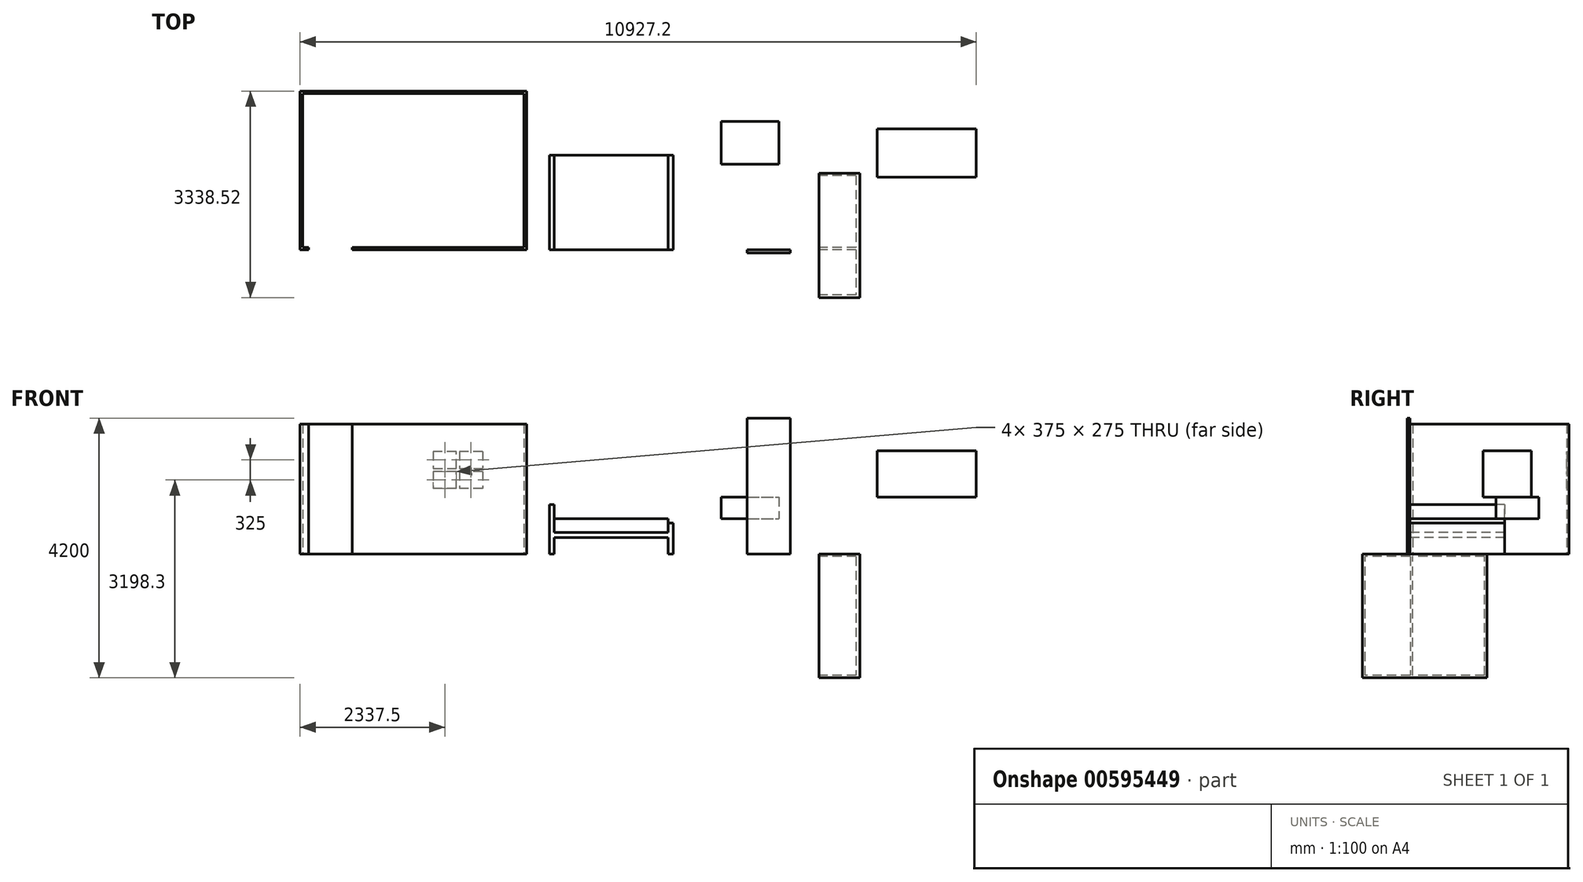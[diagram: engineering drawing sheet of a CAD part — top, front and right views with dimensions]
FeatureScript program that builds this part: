
annotation { "Feature Type Name" : "Feature", "Feature Type Description" : "" }
export const myFeature = defineFeature(function(context is Context, id is Id, definition is map)
    precondition{}
    {
        {
            var Q0;
            Q0=qCreatedBy(makeId("Top.planeOp"),FACE);
            var sketch = newSketch(context, id + "F0", { "sketchPlane" : qUnion([Q0])});
            skLineSegment(sketch, "E0", {"start": v(40, -40) * mm, "end": v(40, -2529) * mm});
            skLineSegment(sketch, "E1", {"start": v(40, -2529) * mm, "end": v(140, -2529) * mm});
            skLineSegment(sketch, "E2", {"start": v(140, -2529) * mm, "end": v(140, -2569) * mm});
            skLineSegment(sketch, "E3", {"start": v(840, -2529) * mm, "end": v(3620, -2529) * mm});
            skLineSegment(sketch, "E4", {"start": v(3620, -2529) * mm, "end": v(3620, -40) * mm});
            skLineSegment(sketch, "E5", {"start": v(3620, -40) * mm, "end": v(40, -40) * mm});
            skLineSegment(sketch, "E6.0", {"start": v(0, -2569) * mm, "end": v(140, -2569) * mm});
            skLineSegment(sketch, "E6.1", {"start": v(0, 0) * mm, "end": v(0, -2569) * mm});
            skLineSegment(sketch, "E6.2", {"start": v(840, -2569) * mm, "end": v(840, -2529) * mm});
            skLineSegment(sketch, "E6.3", {"start": v(840, -2569) * mm, "end": v(3660, -2569) * mm});
            skLineSegment(sketch, "E6.4", {"start": v(3660, -2569) * mm, "end": v(3660, 0) * mm});
            skLineSegment(sketch, "E6.5", {"start": v(3660, 0) * mm, "end": v(0, 0) * mm});
            skLineSegment(sketch, "E7", {"start": v(77.43, -3008.4) * mm, "end": v(77.43, -5573.82) * mm});
            skLineSegment(sketch, "E8", {"start": v(77.43, -5573.82) * mm, "end": v(3731.87, -5573.82) * mm});
            skLineSegment(sketch, "E9", {"start": v(3731.87, -5573.82) * mm, "end": v(3731.87, -3584.3) * mm});
            skLineSegment(sketch, "E10", {"start": v(3731.87, -3584.3) * mm, "end": v(865.25, -3584.3) * mm});
            skLineSegment(sketch, "E11", {"start": v(865.25, -3584.3) * mm, "end": v(865.25, -3010.27) * mm});
            skSolve(sketch);
        }
        {
            var Q0;
            Q0 = qSketchRegion(id + "F0", true);
            extrude(context, id + "F1", {"entities" : qUnion([Q0]), "depth" : 2100 * mm, "offsetDistance" : 25 * mm});
        }
        {
            var Q0;
            Q0=makeQuery(id+"F1.opExtrude","SWEPT_FACE",FACE,{"disambiguationData":[OSD([sQuery(id+"F0.wireOp",EDGE,"E6.3")])]});
            var sketch = newSketch(context, id + "F2", { "sketchPlane" : qUnion([Q0])});
            skLineSegment(sketch, "E12", {"start": v(4029.05, 800) * mm, "end": v(4029.05, 0) * mm});
            skLineSegment(sketch, "E13", {"start": v(4029.05, 0) * mm, "end": v(4109.05, 0) * mm});
            skLineSegment(sketch, "E14", {"start": v(4109.05, 0) * mm, "end": v(4109.05, 270) * mm});
            skLineSegment(sketch, "E15", {"start": v(4109.05, 270) * mm, "end": v(5949.05, 270) * mm});
            skLineSegment(sketch, "E16", {"start": v(5949.05, 270) * mm, "end": v(5949.05, 0) * mm});
            skLineSegment(sketch, "E17", {"start": v(5949.05, 0) * mm, "end": v(6029.05, 0) * mm});
            skLineSegment(sketch, "E18", {"start": v(6029.05, 0) * mm, "end": v(6029.05, 500) * mm});
            skLineSegment(sketch, "E19", {"start": v(6029.05, 500) * mm, "end": v(5949.05, 500) * mm});
            skLineSegment(sketch, "E20", {"start": v(5949.05, 500) * mm, "end": v(5949.05, 350) * mm});
            skLineSegment(sketch, "E21", {"start": v(5949.05, 350) * mm, "end": v(4109.05, 350) * mm});
            skLineSegment(sketch, "E22", {"start": v(4109.05, 350) * mm, "end": v(4109.05, 800) * mm});
            skLineSegment(sketch, "E23", {"start": v(4109.05, 800) * mm, "end": v(4029.05, 800) * mm});
            skSolve(sketch);
        }
        {
            var Q0;
            Q0 = qSketchRegion(id + "F2", true);
            extrude(context, id + "F3", {"entities" : qUnion([Q0]), "oppositeDirection" : true, "depth" : 1530 * mm, "offsetDistance" : 25 * mm});
        }
        {
            var Q0;
            Q0=makeQuery(id+"F1.opExtrude","SWEPT_FACE",FACE,{"disambiguationData":[OSD([sQuery(id+"F0.wireOp",EDGE,"E6.3")])]});
            var sketch = newSketch(context, id + "F4", { "sketchPlane" : qUnion([Q0])});
            skLineSegment(sketch, "E24.bottom", {"start": v(7222.52, 2200) * mm, "end": v(7922.52, 2200) * mm});
            skLineSegment(sketch, "E24.top", {"start": v(7222.52, 0) * mm, "end": v(7922.52, 0) * mm});
            skLineSegment(sketch, "E24.left", {"start": v(7222.52, 2200) * mm, "end": v(7222.52, 0) * mm});
            skLineSegment(sketch, "E24.right", {"start": v(7922.52, 2200) * mm, "end": v(7922.52, 0) * mm});
            skSolve(sketch);
        }
        {
            var Q0;
            Q0 = qSketchRegion(id + "F4", true);
            extrude(context, id + "F5", {"entities" : qUnion([Q0]), "depth" : 50 * mm, "offsetDistance" : 25 * mm});
        }
        {
            var Q0;
            Q0=makeQuery(id+"F1.opExtrude","SWEPT_FACE",FACE,{"disambiguationData":[OSD([sQuery(id+"F0.wireOp",EDGE,"E6.5")])]});
            var sketch = newSketch(context, id + "F6", { "sketchPlane" : qUnion([Q0])});
            skLineSegment(sketch, "E25.bottom", {"start": v(-2950, 1660.8) * mm, "end": v(-2575, 1660.8) * mm});
            skLineSegment(sketch, "E25.top", {"start": v(-2950, 1060.8) * mm, "end": v(-2575, 1060.8) * mm});
            skLineSegment(sketch, "E25.left", {"start": v(-2950, 1660.8) * mm, "end": v(-2950, 1385.8) * mm});
            skLineSegment(sketch, "E25.right", {"start": v(-2150, 1660.8) * mm, "end": v(-2150, 1385.8) * mm});
            skLineSegment(sketch, "E26", {"start": v(-2575, 1660.8) * mm, "end": v(-2575, 1385.8) * mm});
            skLineSegment(sketch, "E27", {"start": v(-2575, 1385.8) * mm, "end": v(-2950, 1385.8) * mm});
            skLineSegment(sketch, "E28", {"start": v(-2950, 1335.8) * mm, "end": v(-2575, 1335.8) * mm});
            skLineSegment(sketch, "E29", {"start": v(-2575, 1335.8) * mm, "end": v(-2575, 1060.8) * mm});
            skLineSegment(sketch, "E30", {"start": v(-2525, 1060.8) * mm, "end": v(-2525, 1335.8) * mm});
            skLineSegment(sketch, "E31", {"start": v(-2525, 1335.8) * mm, "end": v(-2150, 1335.8) * mm});
            skLineSegment(sketch, "E32", {"start": v(-2150, 1385.8) * mm, "end": v(-2525, 1385.8) * mm});
            skLineSegment(sketch, "E33", {"start": v(-2525, 1385.8) * mm, "end": v(-2525, 1660.8) * mm});
            skLineSegment(sketch, "E34.trimOffspring", {"start": v(-2525, 1660.8) * mm, "end": v(-2150, 1660.8) * mm});
            skLineSegment(sketch, "E35.trimOffspring", {"start": v(-2150, 1335.8) * mm, "end": v(-2150, 1060.8) * mm});
            skLineSegment(sketch, "E36.trimOffspring", {"start": v(-2950, 1335.8) * mm, "end": v(-2950, 1060.8) * mm});
            skLineSegment(sketch, "E37.trimOffspring", {"start": v(-2525, 1060.8) * mm, "end": v(-2150, 1060.8) * mm});
            skLineSegment(sketch, "E38", {"start": v(-2950, 1335.8) * mm, "end": v(-2950, 1385.8) * mm});
            skLineSegment(sketch, "E39", {"start": v(-2525, 1060.8) * mm, "end": v(-2575, 1060.8) * mm});
            skLineSegment(sketch, "E40", {"start": v(-2150, 1335.8) * mm, "end": v(-2150, 1385.8) * mm});
            skLineSegment(sketch, "E41", {"start": v(-2525, 1660.8) * mm, "end": v(-2575, 1660.8) * mm});
            skSolve(sketch);
        }
        {
            var Q0;
            {var subQ3=sQuery(id+"F6.wireOp",EDGE,"E26");Q0=makeQuery(id+"F6.imprint","IMPRINT",FACE,{"disambiguationData":[TD([[makeQuery(id+"F6.imprint","IMPRINT",EDGE,{"derivedFrom":subQ3}),-1.0]])]});}
            var Q1;
            {var subQ4=sQuery(id+"F6.wireOp",EDGE,"E32");Q1=makeQuery(id+"F6.imprint","IMPRINT",FACE,{"disambiguationData":[TD([[makeQuery(id+"F6.imprint","IMPRINT",EDGE,{"derivedFrom":subQ4}),-1.0]])]});}
            var Q2;
            {var subQ4=sQuery(id+"F6.wireOp",EDGE,"E28");Q2=makeQuery(id+"F6.imprint","IMPRINT",FACE,{"disambiguationData":[TD([[makeQuery(id+"F6.imprint","IMPRINT",EDGE,{"derivedFrom":subQ4}),-1.0]])]});}
            var Q3;
            {var subQ3=sQuery(id+"F6.wireOp",EDGE,"E30");Q3=makeQuery(id+"F6.imprint","IMPRINT",FACE,{"disambiguationData":[TD([[makeQuery(id+"F6.imprint","IMPRINT",EDGE,{"derivedFrom":subQ3}),-1.0]])]});}
            extrude(context, id + "F7", {"entities" : qUnion([Q0, Q1, Q2, Q3]), "operationType" : NewBodyOperationType.REMOVE, "oppositeDirection" : true, "depth" : 100 * mm, "offsetDistance" : 25 * mm});
        }
        {
            var Q0;
            Q0=makeQuery(id+"F1.opExtrude","CAP_FACE",FACE,{"disambiguationData":[OSD([sQuery(id+"F0.wireOp",EDGE,"E0"),sQuery(id+"F0.wireOp",EDGE,"E1"),sQuery(id+"F0.wireOp",EDGE,"E2"),sQuery(id+"F0.wireOp",EDGE,"E3"),sQuery(id+"F0.wireOp",EDGE,"E4"),sQuery(id+"F0.wireOp",EDGE,"E5"),sQuery(id+"F0.wireOp",EDGE,"E6.0"),sQuery(id+"F0.wireOp",EDGE,"E6.1"),sQuery(id+"F0.wireOp",EDGE,"E6.2"),sQuery(id+"F0.wireOp",EDGE,"E6.3"),sQuery(id+"F0.wireOp",EDGE,"E6.4"),sQuery(id+"F0.wireOp",EDGE,"E6.5")])],"isStart":true});
            var sketch = newSketch(context, id + "F8", { "sketchPlane" : qUnion([Q0])});
            skLineSegment(sketch, "E42.bottom", {"start": v(8384.36, 1328.52) * mm, "end": v(9044.36, 1328.52) * mm});
            skLineSegment(sketch, "E42.top", {"start": v(8384.36, 3338.52) * mm, "end": v(9044.36, 3338.52) * mm});
            skLineSegment(sketch, "E42.left", {"start": v(8384.36, 1328.52) * mm, "end": v(8384.36, 3338.52) * mm});
            skLineSegment(sketch, "E42.right", {"start": v(9044.36, 1328.52) * mm, "end": v(9044.36, 3338.52) * mm});
            skSolve(sketch);
        }
        {
            var Q0;
            Q0 = qSketchRegion(id + "F8", true);
            extrude(context, id + "F9", {"entities" : qUnion([Q0]), "depth" : 2000 * mm, "offsetDistance" : 25 * mm});
        }
        {
            var Q0;
            Q0=makeQuery(id+"F9.opExtrude","SWEPT_FACE",FACE,{"disambiguationData":[OSD([sQuery(id+"F8.wireOp",EDGE,"E42.left")])]});
            var sketch = newSketch(context, id + "F10", { "sketchPlane" : qUnion([Q0])});
            skLineSegment(sketch, "E43.0", {"start": v(1368.52, -40) * mm, "end": v(2526.92, -40) * mm});
            skLineSegment(sketch, "E43.1", {"start": v(1368.52, -1960) * mm, "end": v(1368.52, -40) * mm});
            skLineSegment(sketch, "E43.2", {"start": v(1368.52, -1960) * mm, "end": v(2526.92, -1960) * mm});
            skLineSegment(sketch, "E43.3", {"start": v(3298.52, -1960) * mm, "end": v(3298.52, -40) * mm});
            skLineSegment(sketch, "E44", {"start": v(2526.92, -1960) * mm, "end": v(2526.92, -40) * mm});
            skLineSegment(sketch, "E45", {"start": v(2566.92, -40) * mm, "end": v(2566.92, -1960) * mm});
            skLineSegment(sketch, "E46.trimOffspring", {"start": v(2566.92, -40) * mm, "end": v(3298.52, -40) * mm});
            skLineSegment(sketch, "E47.trimOffspring", {"start": v(2566.92, -1960) * mm, "end": v(3298.52, -1960) * mm});
            skSolve(sketch);
        }
        {
            var Q0;
            Q0=makeQuery(id+"F10.imprint","IMPRINT",FACE,{"disambiguationData":[TD([[makeQuery(id+"F10.imprint","IMPRINT",EDGE,{"derivedFrom":sQuery(id+"F10.wireOp",EDGE,"E43.0")}),-1.0]])]});
            var Q1;
            Q1=makeQuery(id+"F10.imprint","IMPRINT",FACE,{"disambiguationData":[TD([[makeQuery(id+"F10.imprint","IMPRINT",EDGE,{"derivedFrom":sQuery(id+"F10.wireOp",EDGE,"E43.3")}),1.0]])]});
            extrude(context, id + "F11", {"entities" : qUnion([Q0, Q1]), "operationType" : NewBodyOperationType.REMOVE, "oppositeDirection" : true, "depth" : 600 * mm, "offsetDistance" : 25 * mm});
        }
        {
            var Q0;
            Q0=makeQuery(id+"F3.opExtrude","CAP_FACE",FACE,{"disambiguationData":[OSD([sQuery(id+"F2.wireOp",EDGE,"E12"),sQuery(id+"F2.wireOp",EDGE,"E13"),sQuery(id+"F2.wireOp",EDGE,"E14"),sQuery(id+"F2.wireOp",EDGE,"E15"),sQuery(id+"F2.wireOp",EDGE,"E16"),sQuery(id+"F2.wireOp",EDGE,"E17"),sQuery(id+"F2.wireOp",EDGE,"E18"),sQuery(id+"F2.wireOp",EDGE,"E19"),sQuery(id+"F2.wireOp",EDGE,"E20"),sQuery(id+"F2.wireOp",EDGE,"E21"),sQuery(id+"F2.wireOp",EDGE,"E22"),sQuery(id+"F2.wireOp",EDGE,"E23")])],"isStart":true});
            var sketch = newSketch(context, id + "F12", { "sketchPlane" : qUnion([Q0])});
            skLineSegment(sketch, "E48.bottom", {"start": v(4109.05, 570) * mm, "end": v(5949.05, 570) * mm});
            skLineSegment(sketch, "E48.top", {"start": v(4109.05, 350) * mm, "end": v(5949.05, 350) * mm});
            skLineSegment(sketch, "E48.left", {"start": v(4109.05, 570) * mm, "end": v(4109.05, 350) * mm});
            skLineSegment(sketch, "E48.right", {"start": v(5949.05, 570) * mm, "end": v(5949.05, 350) * mm});
            skSolve(sketch);
        }
        {
            var Q0;
            Q0 = qSketchRegion(id + "F12", true);
            var Q1;
            Q1=makeQuery(id+"F3.opExtrude","CAP_FACE",FACE,{"disambiguationData":[OSD([sQuery(id+"F2.wireOp",EDGE,"E12"),sQuery(id+"F2.wireOp",EDGE,"E13"),sQuery(id+"F2.wireOp",EDGE,"E14"),sQuery(id+"F2.wireOp",EDGE,"E15"),sQuery(id+"F2.wireOp",EDGE,"E16"),sQuery(id+"F2.wireOp",EDGE,"E17"),sQuery(id+"F2.wireOp",EDGE,"E18"),sQuery(id+"F2.wireOp",EDGE,"E19"),sQuery(id+"F2.wireOp",EDGE,"E20"),sQuery(id+"F2.wireOp",EDGE,"E21"),sQuery(id+"F2.wireOp",EDGE,"E22"),sQuery(id+"F2.wireOp",EDGE,"E23")])],"isStart":false});
            extrude(context, id + "F13", {"entities" : qUnion([Q0]), "endBound" : BoundingType.UP_TO_SURFACE, "oppositeDirection" : true, "depth" : 1500 * mm, "endBoundEntityFace" : qUnion([Q1]), "offsetDistance" : 25 * mm});
        }
        {
            var Q0;
            Q0=makeQuery(id+"F13.opExtrude","SWEPT_FACE",FACE,{"disambiguationData":[OSD([sQuery(id+"F12.wireOp",EDGE,"E48.bottom")])]});
            var sketch = newSketch(context, id + "F14", { "sketchPlane" : qUnion([Q0])});
            skLineSegment(sketch, "E49.bottom", {"start": v(6807.34, -490.43) * mm, "end": v(7737.34, -490.43) * mm});
            skLineSegment(sketch, "E49.top", {"start": v(6807.34, -1180.43) * mm, "end": v(7737.34, -1180.43) * mm});
            skLineSegment(sketch, "E49.left", {"start": v(6807.34, -490.43) * mm, "end": v(6807.34, -1180.43) * mm});
            skLineSegment(sketch, "E49.right", {"start": v(7737.34, -490.43) * mm, "end": v(7737.34, -1180.43) * mm});
            skSolve(sketch);
        }
        {
            var Q0;
            Q0=makeQuery(id+"F14.imprint","IMPRINT",FACE,{"disambiguationData":[TD([[makeQuery(id+"F14.imprint","IMPRINT",EDGE,{"derivedFrom":sQuery(id+"F14.wireOp",EDGE,"E49.bottom")}),-1.0]])]});
            extrude(context, id + "F15", {"entities" : qUnion([Q0]), "depth" : 350 * mm, "offsetDistance" : 25 * mm});
        }
        {
            var Q0;
            Q0=makeQuery(id+"F15.opExtrude","CAP_FACE",FACE,{"disambiguationData":[OSD([sQuery(id+"F14.wireOp",EDGE,"E49.bottom"),sQuery(id+"F14.wireOp",EDGE,"E49.top"),sQuery(id+"F14.wireOp",EDGE,"E49.left"),sQuery(id+"F14.wireOp",EDGE,"E49.right")])],"isStart":false});
            var sketch = newSketch(context, id + "F16", { "sketchPlane" : qUnion([Q0])});
            skLineSegment(sketch, "E50.bottom", {"start": v(9327.25, -612.53) * mm, "end": v(10927.25, -612.53) * mm});
            skLineSegment(sketch, "E50.top", {"start": v(9327.25, -1392.53) * mm, "end": v(10927.25, -1392.53) * mm});
            skLineSegment(sketch, "E50.left", {"start": v(9327.25, -612.53) * mm, "end": v(9327.25, -1392.53) * mm});
            skLineSegment(sketch, "E50.right", {"start": v(10927.25, -612.53) * mm, "end": v(10927.25, -1392.53) * mm});
            skSolve(sketch);
        }
        {
            var Q0;
            Q0=makeQuery(id+"F16.imprint","IMPRINT",FACE,{"disambiguationData":[TD([[makeQuery(id+"F16.imprint","IMPRINT",EDGE,{"derivedFrom":sQuery(id+"F16.wireOp",EDGE,"E50.bottom")}),-1.0]])]});
            extrude(context, id + "F17", {"entities" : qUnion([Q0]), "depth" : 750 * mm, "offsetDistance" : 25 * mm});
        }
    });
